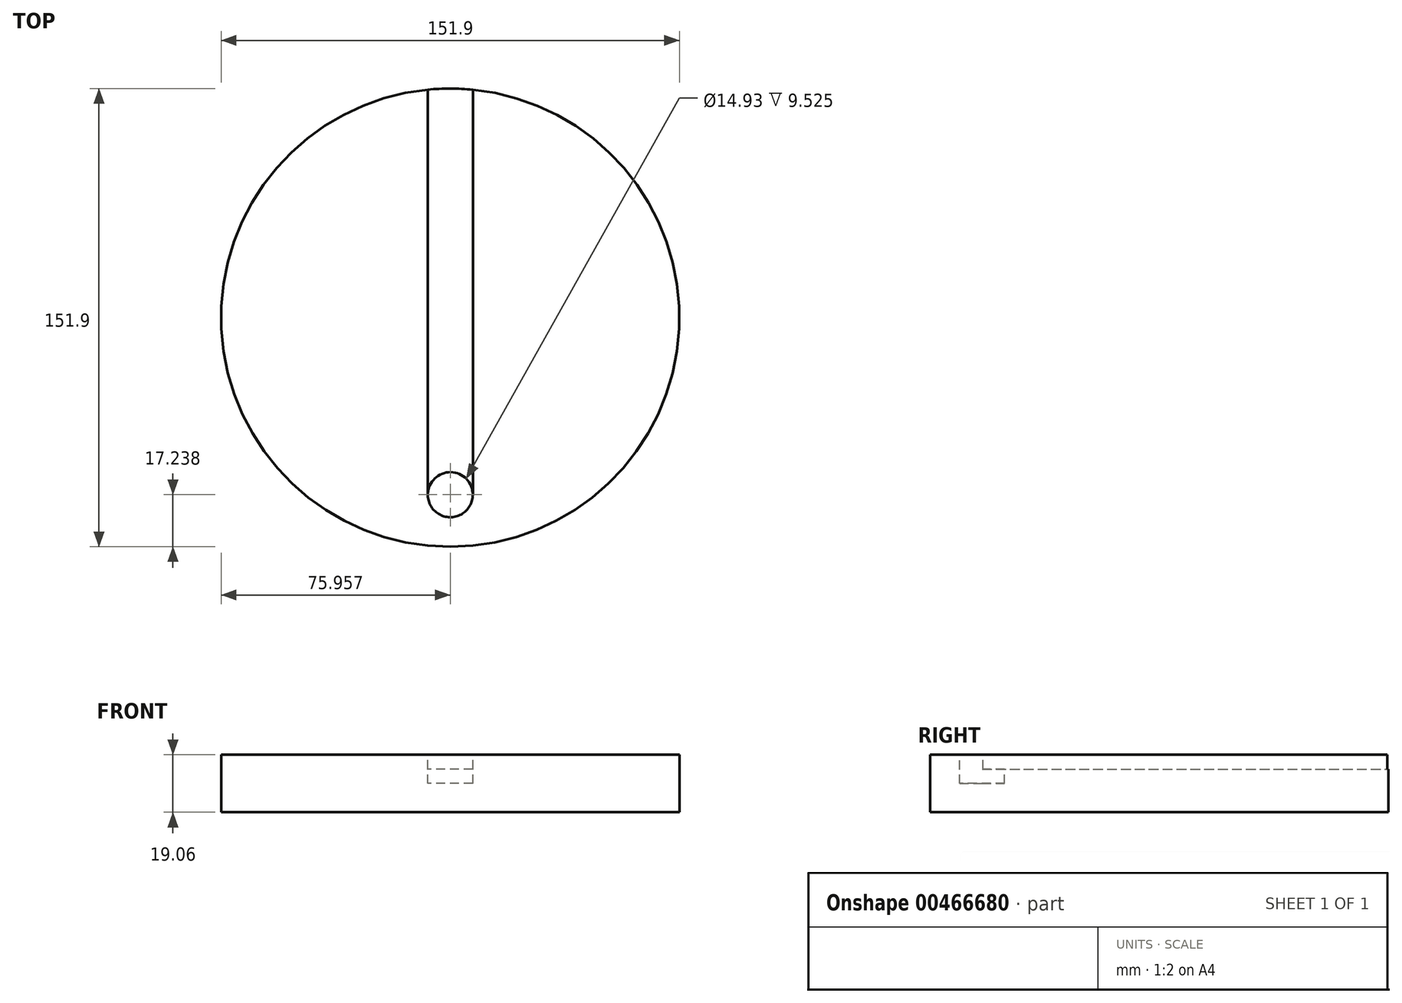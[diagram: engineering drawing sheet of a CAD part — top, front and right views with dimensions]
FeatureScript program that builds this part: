
annotation { "Feature Type Name" : "Feature", "Feature Type Description" : "" }
export const myFeature = defineFeature(function(context is Context, id is Id, definition is map)
    precondition{}
    {
        {
            var Q0;
            Q0=qCreatedBy(makeId("Top.planeOp"),FACE);
            var sketch = newSketch(context, id + "F0", { "sketchPlane" : qUnion([Q0])});
            skCircle(sketch, "E0", {"center": v(0, 0) * mm, "radius": 75.95 * mm});
            skSolve(sketch);
        }
        {
            var Q0;
            Q0=makeQuery(id+"F0.imprint","IMPRINT",FACE,{"disambiguationData":[TD([[makeQuery(id+"F0.imprint","IMPRINT",EDGE,{"derivedFrom":sQuery(id+"F0.wireOp",EDGE,"E0")}),1.0]])]});
            extrude(context, id + "F1", {"entities" : qUnion([Q0]), "endBound" : BoundingType.SYMMETRIC, "depth" : 19.05 * mm});
        }
        {
            var Q0;
            Q0=makeQuery(id+"F1.opExtrude","CAP_FACE",FACE,{"disambiguationData":[OSD([sQuery(id+"F0.wireOp",EDGE,"E0")])],"isStart":false});
            var sketch = newSketch(context, id + "F2", { "sketchPlane" : qUnion([Q0])});
            skArc(sketch, "E1", {"start": v(-7.45, -58.44) * mm, "mid": v(-0.13, -66.18) * mm, "end": v(7.47, -58.71) * mm});
            skLineSegment(sketch, "E2", {"start": v(-7.45, -58.99) * mm, "end": v(-7.45, 75.59) * mm});
            skLineSegment(sketch, "E3", {"start": v(7.47, -58.71) * mm, "end": v(7.47, 75.59) * mm});
            skSolve(sketch);
        }
        {
            var Q0;
            Q0 = qSketchRegion(id + "F2", true);
            var Q1;
            {var subQ0=sQuery(id+"F2.wireOp",EDGE,"E3");Q1=makeQuery(id+"F2.imprint","IMPRINT",FACE,{"disambiguationData":[TD([[makeQuery(id+"F2.imprint","IMPRINT",EDGE,{"derivedFrom":subQ0}),1.0]])]});}
            extrude(context, id + "F3", {"entities" : qUnion([Q0, Q1]), "operationType" : NewBodyOperationType.REMOVE, "oppositeDirection" : true, "depth" : 4.75 * mm, "offsetDistance" : 25.4 * mm});
        }
        {
            var Q0;
            Q0=makeQuery(id+"F1.opExtrude","CAP_FACE",FACE,{"disambiguationData":[OSD([sQuery(id+"F0.wireOp",EDGE,"E0")])],"isStart":false});
            var sketch = newSketch(context, id + "F4", { "sketchPlane" : qUnion([Q0])});
            skCircle(sketch, "E4", {"center": v(0, -58.71) * mm, "radius": 7.47 * mm});
            skSolve(sketch);
        }
        {
            var Q0;
            Q0 = qSketchRegion(id + "F4", true);
            extrude(context, id + "F5", {"entities" : qUnion([Q0]), "operationType" : NewBodyOperationType.REMOVE, "oppositeDirection" : true, "depth" : 9.52 * mm, "offsetDistance" : 25.4 * mm});
        }
    });
